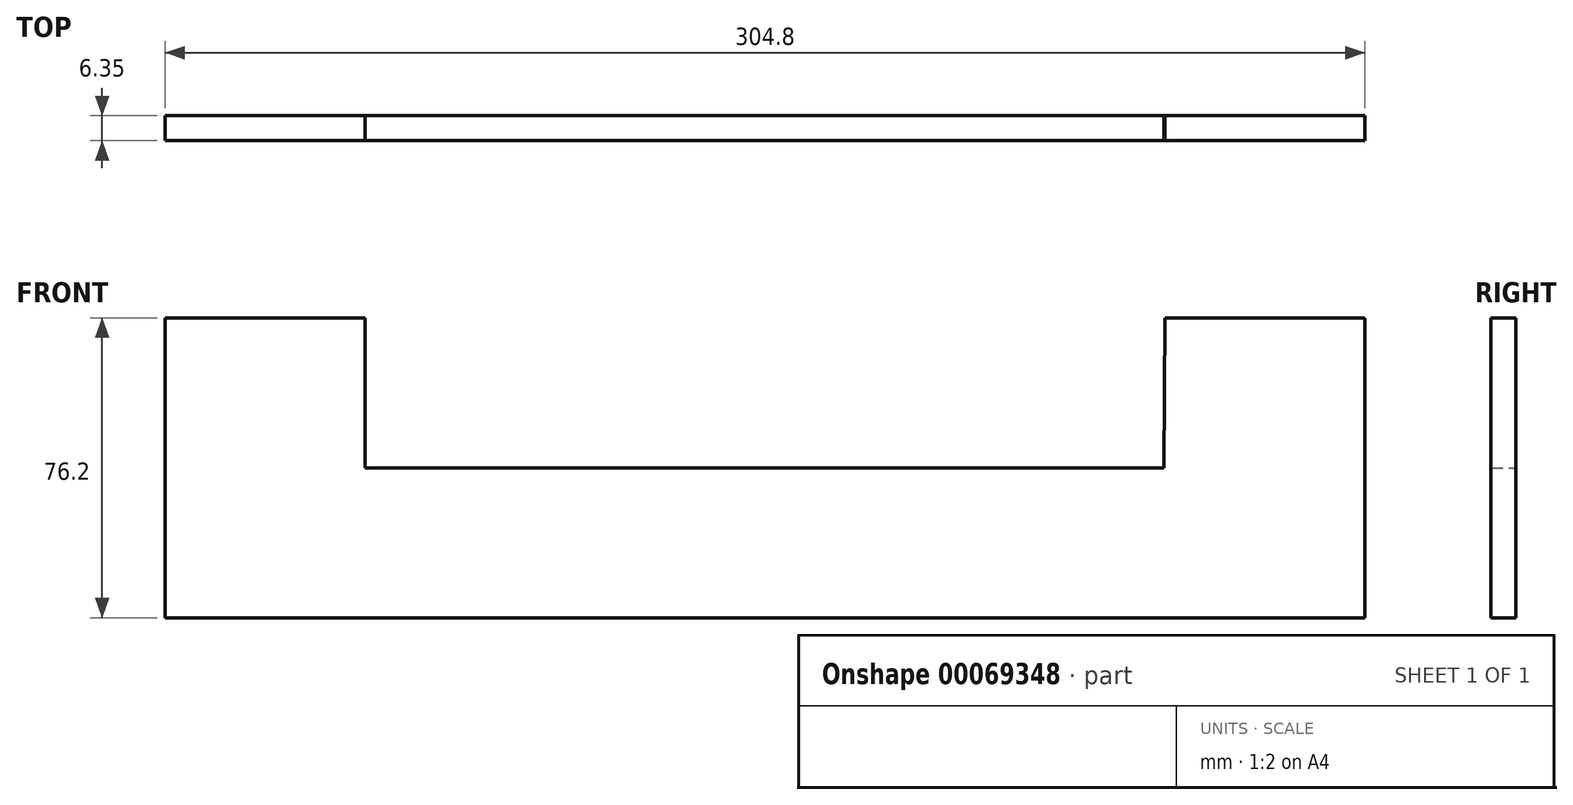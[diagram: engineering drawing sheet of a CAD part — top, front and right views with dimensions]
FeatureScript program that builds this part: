
annotation { "Feature Type Name" : "Feature", "Feature Type Description" : "" }
export const myFeature = defineFeature(function(context is Context, id is Id, definition is map)
    precondition{}
    {
        {
            var Q0;
            Q0=qCreatedBy(makeId("Front.planeOp"),FACE);
            var sketch = newSketch(context, id + "F0", { "sketchPlane" : qUnion([Q0])});
            skLineSegment(sketch, "E0", {"start": v(-50.8, 38.1) * mm, "end": v(-50.8, -38.1) * mm});
            skLineSegment(sketch, "E1", {"start": v(-50.8, -38.1) * mm, "end": v(254, -38.1) * mm});
            skLineSegment(sketch, "E2", {"start": v(254, -38.1) * mm, "end": v(254, 38.1) * mm});
            skLineSegment(sketch, "E3", {"start": v(-50.8, 38.1) * mm, "end": v(0, 38.1) * mm});
            skLineSegment(sketch, "E4", {"start": v(254, 38.1) * mm, "end": v(203.2, 38.1) * mm});
            skLineSegment(sketch, "E5", {"start": v(0, 38.1) * mm, "end": v(0, 0) * mm});
            skLineSegment(sketch, "E6", {"start": v(0, 0) * mm, "end": v(203, 0) * mm});
            skLineSegment(sketch, "E7", {"start": v(203.2, 38.1) * mm, "end": v(203, 0) * mm});
            skSolve(sketch);
        }
        {
            var Q0;
            Q0=qSketchRegion(id+"F0",true);
            extrude(context, id + "F1", {"entities" : qUnion([Q0]), "depth" : 6.35 * mm});
        }
    });
